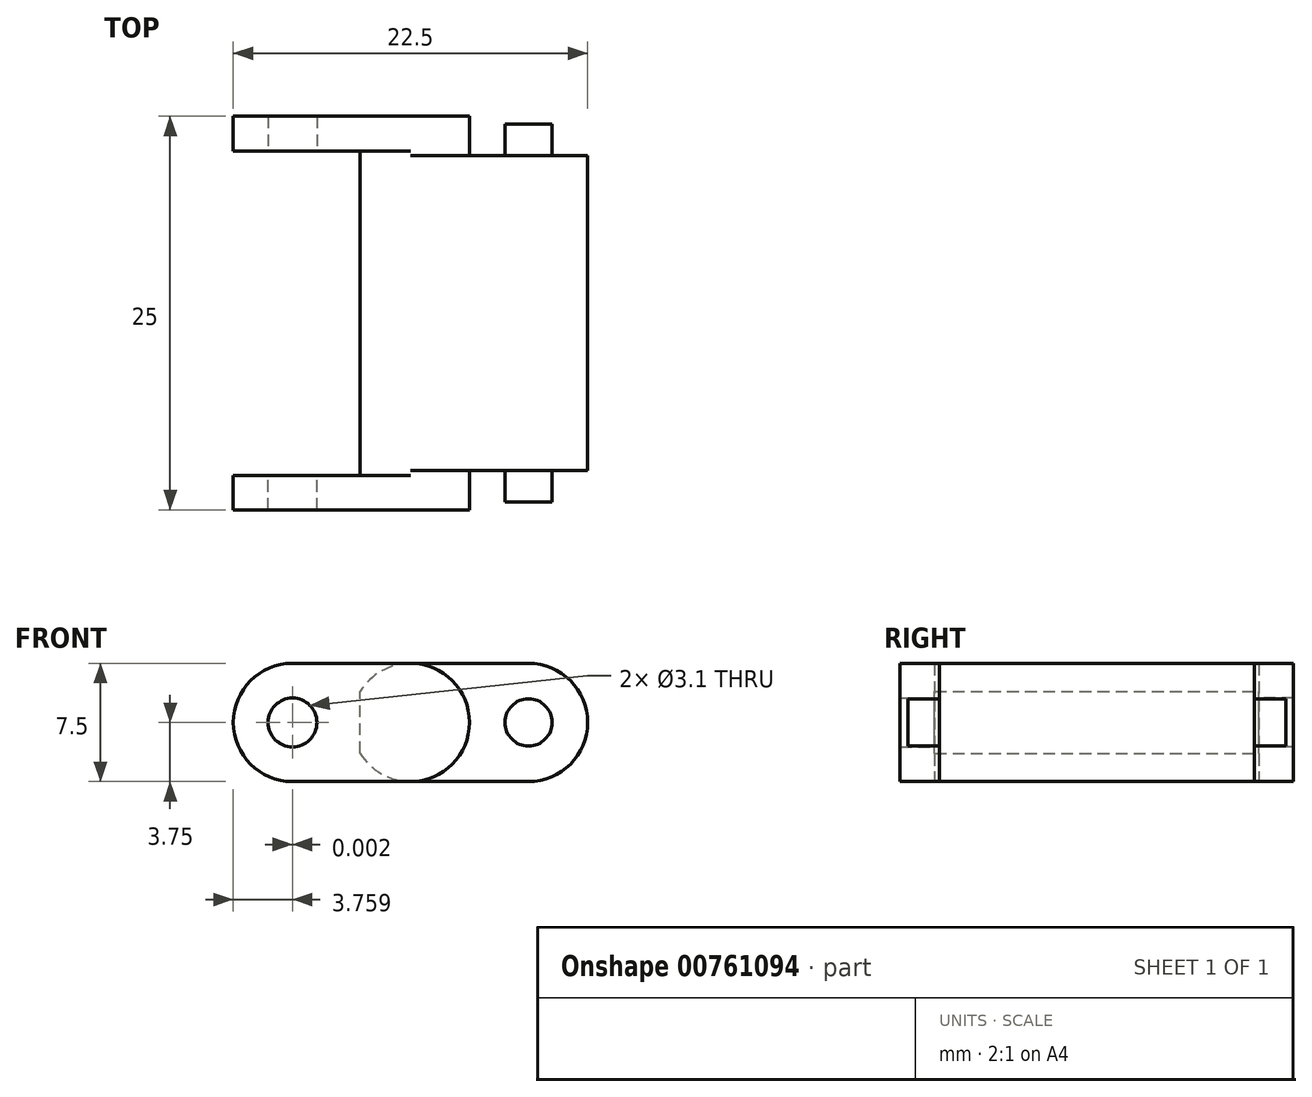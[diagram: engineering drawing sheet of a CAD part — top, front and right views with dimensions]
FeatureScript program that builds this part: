
annotation { "Feature Type Name" : "Feature", "Feature Type Description" : "" }
export const myFeature = defineFeature(function(context is Context, id is Id, definition is map)
    precondition{}
    {
        {
            var Q0;
            Q0=qCreatedBy(makeId("Front.planeOp"),FACE);
            var sketch = newSketch(context, id + "F0", { "sketchPlane" : qUnion([Q0])});
            skCircle(sketch, "E0", {"center": v(0, 0) * mm, "radius": 3.75 * mm});
            skCircle(sketch, "E1", {"center": v(7.5, 0) * mm, "radius": 3.75 * mm});
            skCircle(sketch, "E2", {"center": v(-7.5, 0) * mm, "radius": 3.75 * mm});
            skLineSegment(sketch, "E3", {"start": v(0, 3.75) * mm, "end": v(7.5, 3.75) * mm});
            skLineSegment(sketch, "E4", {"start": v(0, -3.75) * mm, "end": v(7.5, -3.75) * mm});
            skLineSegment(sketch, "E5", {"start": v(0, 3.75) * mm, "end": v(-7.5, 3.75) * mm});
            skLineSegment(sketch, "E6", {"start": v(0, -3.75) * mm, "end": v(-7.5, -3.75) * mm});
            skSolve(sketch);
        }
        {
            var Q0;
            {var subQ0=sQuery(id+"F0.wireOp",EDGE,"E0");var subQ2=makeQuery(id+"F0.imprint","INTERSECT",VERTEX,{"derivedFrom":[subQ0,sQuery(id+"F0.wireOp",EDGE,"E1")]});Q0=makeQuery(id+"F0.imprint","IMPRINT",FACE,{"disambiguationData":[TD([[makeQuery(id+"F0.imprint","IMPRINT",EDGE,{"disambiguationData":[TD([[subQ2,-1.0]])],"derivedFrom":subQ0}),1.0]])]});}
            var Q1;
            {var subQ0=sQuery(id+"F0.wireOp",EDGE,"E3");Q1=makeQuery(id+"F0.imprint","IMPRINT",FACE,{"disambiguationData":[TD([[makeQuery(id+"F0.imprint","IMPRINT",EDGE,{"derivedFrom":subQ0}),-1.0]])]});}
            var Q2;
            {var subQ0=sQuery(id+"F0.wireOp",EDGE,"E1");var subQ1=makeQuery(id+"F0.imprint","INTERSECT",VERTEX,{"derivedFrom":[subQ0,sQuery(id+"F0.wireOp",EDGE,"E3")]});Q2=makeQuery(id+"F0.imprint","IMPRINT",FACE,{"disambiguationData":[TD([[makeQuery(id+"F0.imprint","IMPRINT",EDGE,{"disambiguationData":[TD([[subQ1,-1.0]])],"derivedFrom":subQ0}),1.0]])]});}
            var Q3;
            {var subQ0=sQuery(id+"F0.wireOp",EDGE,"E4");Q3=makeQuery(id+"F0.imprint","IMPRINT",FACE,{"disambiguationData":[TD([[makeQuery(id+"F0.imprint","IMPRINT",EDGE,{"derivedFrom":subQ0}),1.0]])]});}
            extrude(context, id + "F1", {"entities" : qUnion([Q0, Q1, Q2, Q3]), "endBound" : BoundingType.SYMMETRIC, "depth" : 20 * mm, "offsetDistance" : 25 * mm});
        }
        {
            var Q0;
            {var subQ0=sQuery(id+"F0.wireOp",EDGE,"E2");var subQ1=makeQuery(id+"F0.imprint","INTERSECT",VERTEX,{"derivedFrom":[subQ0,sQuery(id+"F0.wireOp",EDGE,"E5")]});Q0=makeQuery(id+"F0.imprint","IMPRINT",FACE,{"disambiguationData":[TD([[makeQuery(id+"F0.imprint","IMPRINT",EDGE,{"disambiguationData":[TD([[subQ1,1.0]])],"derivedFrom":subQ0}),1.0]])]});}
            var Q1;
            {var subQ0=sQuery(id+"F0.wireOp",EDGE,"E5");Q1=makeQuery(id+"F0.imprint","IMPRINT",FACE,{"disambiguationData":[TD([[makeQuery(id+"F0.imprint","IMPRINT",EDGE,{"derivedFrom":subQ0}),1.0]])]});}
            var Q2;
            {var subQ0=sQuery(id+"F0.wireOp",EDGE,"E0");var subQ2=makeQuery(id+"F0.imprint","INTERSECT",VERTEX,{"derivedFrom":[subQ0,sQuery(id+"F0.wireOp",EDGE,"E1")]});Q2=makeQuery(id+"F0.imprint","IMPRINT",FACE,{"disambiguationData":[TD([[makeQuery(id+"F0.imprint","IMPRINT",EDGE,{"disambiguationData":[TD([[subQ2,-1.0]])],"derivedFrom":subQ0}),1.0]])]});}
            var Q3;
            {var subQ0=sQuery(id+"F0.wireOp",EDGE,"E6");Q3=makeQuery(id+"F0.imprint","IMPRINT",FACE,{"disambiguationData":[TD([[makeQuery(id+"F0.imprint","IMPRINT",EDGE,{"derivedFrom":subQ0}),-1.0]])]});}
            extrude(context, id + "F2", {"entities" : qUnion([Q0, Q1, Q2, Q3]), "operationType" : NewBodyOperationType.ADD, "endBound" : BoundingType.SYMMETRIC, "depth" : 25 * mm, "offsetDistance" : 25 * mm});
        }
        {
            var Q0;
            {var subQ0=sQuery(id+"F0.wireOp",EDGE,"E2");var subQ1=makeQuery(id+"F0.imprint","INTERSECT",VERTEX,{"derivedFrom":[subQ0,sQuery(id+"F0.wireOp",EDGE,"E5")]});Q0=makeQuery(id+"F0.imprint","IMPRINT",FACE,{"disambiguationData":[TD([[makeQuery(id+"F0.imprint","IMPRINT",EDGE,{"disambiguationData":[TD([[subQ1,1.0]])],"derivedFrom":subQ0}),1.0]])]});}
            var Q1;
            {var subQ0=sQuery(id+"F0.wireOp",EDGE,"E6");Q1=makeQuery(id+"F0.imprint","IMPRINT",FACE,{"disambiguationData":[TD([[makeQuery(id+"F0.imprint","IMPRINT",EDGE,{"derivedFrom":subQ0}),-1.0]])]});}
            var Q2;
            {var subQ0=sQuery(id+"F0.wireOp",EDGE,"E5");Q2=makeQuery(id+"F0.imprint","IMPRINT",FACE,{"disambiguationData":[TD([[makeQuery(id+"F0.imprint","IMPRINT",EDGE,{"derivedFrom":subQ0}),1.0]])]});}
            extrude(context, id + "F3", {"entities" : qUnion([Q0, Q1, Q2]), "operationType" : NewBodyOperationType.REMOVE, "endBound" : BoundingType.SYMMETRIC, "depth" : 20.6 * mm, "offsetDistance" : 25 * mm});
        }
        {
            var Q0;
            Q0=makeQuery(id+"F1.opExtrude","CAP_FACE",FACE,{"disambiguationData":[OSD([sQuery(id+"F0.wireOp",EDGE,"E0"),sQuery(id+"F0.wireOp",EDGE,"E1"),sQuery(id+"F0.wireOp",EDGE,"E3"),sQuery(id+"F0.wireOp",EDGE,"E4")])],"isStart":false});
            var sketch = newSketch(context, id + "F4", { "sketchPlane" : qUnion([Q0])});
            skCircle(sketch, "E7", {"center": v(7.5, 0) * mm, "radius": 1.5 * mm});
            skCircle(sketch, "E8", {"center": v(-7.5, 0) * mm, "radius": 1.55 * mm});
            skSolve(sketch);
        }
        {
            var Q0;
            Q0=makeQuery(id+"F4.imprint","IMPRINT",FACE,{"disambiguationData":[TD([[makeQuery(id+"F4.imprint","IMPRINT",EDGE,{"derivedFrom":sQuery(id+"F4.wireOp",EDGE,"E7")}),1.0]])]});
            extrude(context, id + "F5", {"entities" : qUnion([Q0]), "operationType" : NewBodyOperationType.ADD, "depth" : 2 * mm, "offsetDistance" : 25 * mm});
        }
        {
            var Q0;
            Q0=makeQuery(id+"F4.imprint","IMPRINT",FACE,{"disambiguationData":[TD([[makeQuery(id+"F4.imprint","IMPRINT",EDGE,{"derivedFrom":sQuery(id+"F4.wireOp",EDGE,"E8")}),1.0]])]});
            extrude(context, id + "F6", {"entities" : qUnion([Q0]), "operationType" : NewBodyOperationType.REMOVE, "depth" : 5 * mm, "offsetDistance" : 25 * mm});
        }
        {
            var Q0;
            Q0=makeQuery(id+"F1.opExtrude","CAP_FACE",FACE,{"disambiguationData":[OSD([sQuery(id+"F0.wireOp",EDGE,"E0"),sQuery(id+"F0.wireOp",EDGE,"E1"),sQuery(id+"F0.wireOp",EDGE,"E3"),sQuery(id+"F0.wireOp",EDGE,"E4")])],"isStart":true});
            var sketch = newSketch(context, id + "F7", { "sketchPlane" : qUnion([Q0])});
            skCircle(sketch, "E9", {"center": v(-7.5, 0) * mm, "radius": 1.5 * mm});
            skCircle(sketch, "E10", {"center": v(7.49, 0) * mm, "radius": 1.55 * mm});
            skSolve(sketch);
        }
        {
            var Q0;
            Q0=makeQuery(id+"F7.imprint","IMPRINT",FACE,{"disambiguationData":[TD([[makeQuery(id+"F7.imprint","IMPRINT",EDGE,{"derivedFrom":sQuery(id+"F7.wireOp",EDGE,"E9")}),1.0]])]});
            extrude(context, id + "F8", {"entities" : qUnion([Q0]), "operationType" : NewBodyOperationType.ADD, "depth" : 2 * mm, "offsetDistance" : 25 * mm});
        }
        {
            var Q0;
            Q0=makeQuery(id+"F7.imprint","IMPRINT",FACE,{"disambiguationData":[TD([[makeQuery(id+"F7.imprint","IMPRINT",EDGE,{"derivedFrom":sQuery(id+"F7.wireOp",EDGE,"E10")}),1.0]])]});
            extrude(context, id + "F9", {"entities" : qUnion([Q0]), "operationType" : NewBodyOperationType.REMOVE, "depth" : 5 * mm, "offsetDistance" : 25 * mm});
        }
        {
            var Q0;
            Q0=qCreatedBy(makeId("Top.planeOp"),FACE);
            var sketch = newSketch(context, id + "F10", { "sketchPlane" : qUnion([Q0])});
            skLineSegment(sketch, "E11", {"start": v(0, 0) * mm, "end": v(-3.2, 0) * mm, "construction": true});
            skLineSegment(sketch, "E12", {"start": v(-3.2, 0) * mm, "end": v(-3.2, 10.3) * mm});
            skLineSegment(sketch, "E13", {"start": v(-3.2, 10.3) * mm, "end": v(-14.78, 10.3) * mm});
            skLineSegment(sketch, "E14", {"start": v(-14.78, 10.3) * mm, "end": v(-14.78, -10.3) * mm});
            skLineSegment(sketch, "E15", {"start": v(-14.78, -10.3) * mm, "end": v(-3.2, -10.3) * mm});
            skLineSegment(sketch, "E16", {"start": v(-3.2, -10.3) * mm, "end": v(-3.2, 0) * mm});
            skSolve(sketch);
        }
        {
            var Q0;
            Q0=makeQuery(id+"F10.imprint","IMPRINT",FACE,{"disambiguationData":[TD([[makeQuery(id+"F10.imprint","IMPRINT",EDGE,{"derivedFrom":sQuery(id+"F10.wireOp",EDGE,"E12")}),1.0]])]});
            extrude(context, id + "F11", {"entities" : qUnion([Q0]), "operationType" : NewBodyOperationType.REMOVE, "endBound" : BoundingType.SYMMETRIC, "oppositeDirection" : true, "depth" : 25 * mm, "offsetDistance" : 25 * mm});
        }
    });
